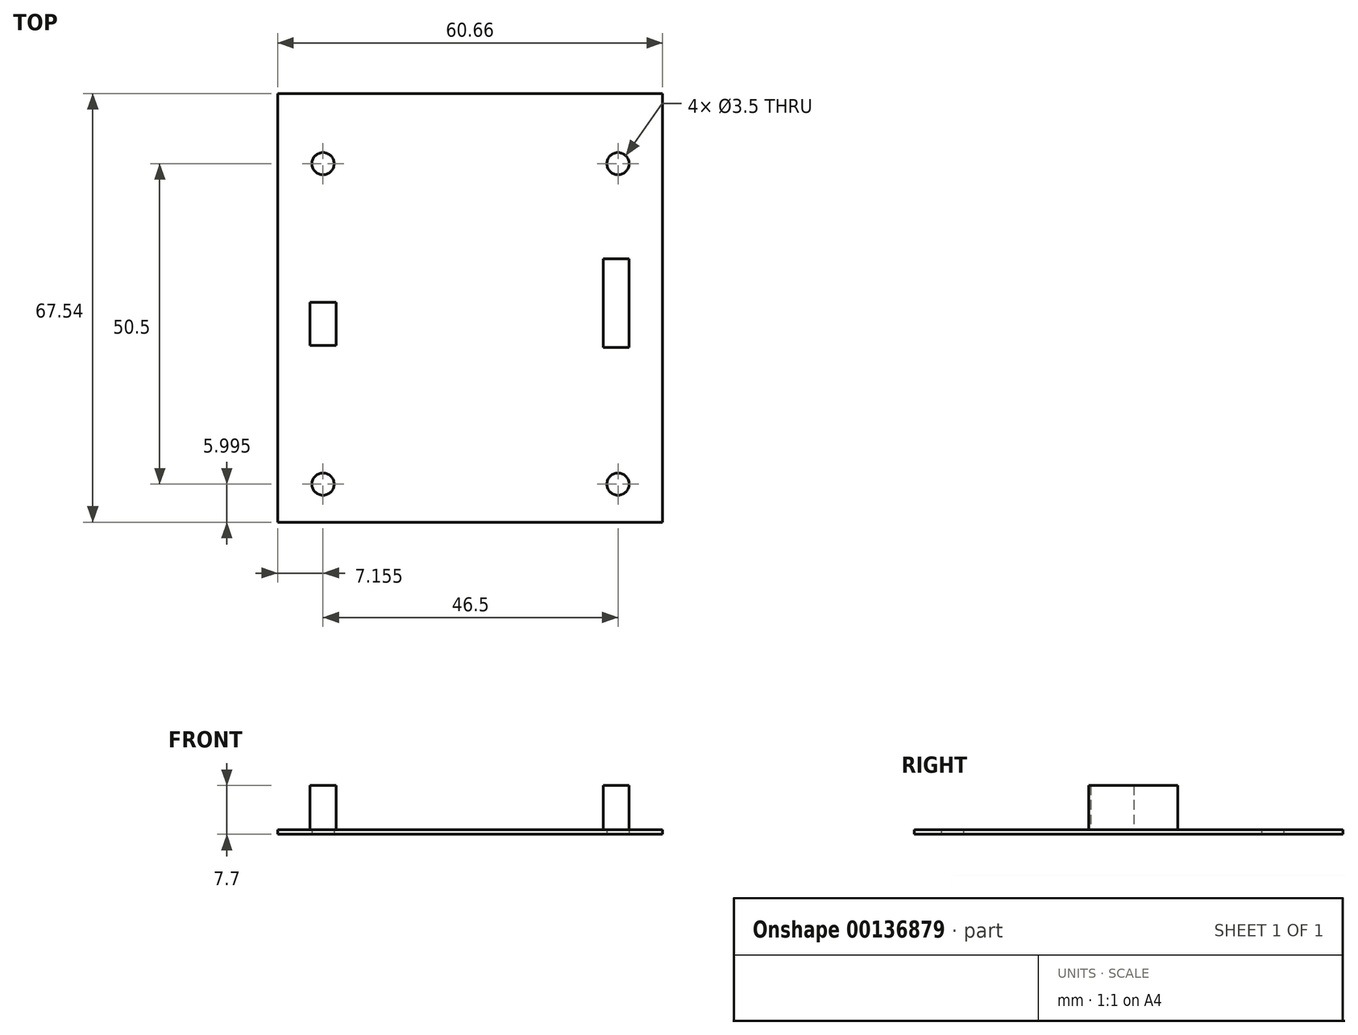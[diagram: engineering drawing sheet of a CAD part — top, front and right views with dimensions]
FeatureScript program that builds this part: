
annotation { "Feature Type Name" : "Feature", "Feature Type Description" : "" }
export const myFeature = defineFeature(function(context is Context, id is Id, definition is map)
    precondition{}
    {
        {
            var Q0;
            Q0=qCreatedBy(makeId("Top.planeOp"),FACE);
            var sketch = newSketch(context, id + "F0", { "sketchPlane" : qUnion([Q0])});
            skLineSegment(sketch, "E0.bottom", {"start": v(-30.32, 33.77) * mm, "end": v(30.33, 33.77) * mm});
            skLineSegment(sketch, "E0.top", {"start": v(-30.33, -33.77) * mm, "end": v(30.32, -33.77) * mm});
            skLineSegment(sketch, "E0.left", {"start": v(-30.32, 33.77) * mm, "end": v(-30.33, -33.77) * mm});
            skLineSegment(sketch, "E0.right", {"start": v(30.33, 33.77) * mm, "end": v(30.32, -33.77) * mm});
            skPoint(sketch, "E0.middle", {"position": v(0, 0) * mm});
            skCircle(sketch, "E1", {"center": v(23.32, -27.77) * mm, "radius": 1.75 * mm});
            skCircle(sketch, "E2", {"center": v(-23.18, -27.77) * mm, "radius": 1.75 * mm});
            skCircle(sketch, "E3", {"center": v(23.32, 22.73) * mm, "radius": 1.75 * mm});
            skCircle(sketch, "E4", {"center": v(-23.18, 22.73) * mm, "radius": 1.75 * mm});
            skSolve(sketch);
        }
        {
            var Q0;
            Q0=makeQuery(id+"F0.imprint","IMPRINT",FACE,{"disambiguationData":[TD([[makeQuery(id+"F0.imprint","IMPRINT",EDGE,{"derivedFrom":sQuery(id+"F0.wireOp",EDGE,"E0.bottom")}),-1.0]])]});
            extrude(context, id + "F1", {"entities" : qUnion([Q0]), "depth" : 0.7 * mm});
        }
        {
            var Q0;
            Q0=makeQuery(id+"F1.opExtrude","CAP_FACE",FACE,{"disambiguationData":[OSD([sQuery(id+"F0.wireOp",EDGE,"E0.bottom"),sQuery(id+"F0.wireOp",EDGE,"E0.top"),sQuery(id+"F0.wireOp",EDGE,"E0.left"),sQuery(id+"F0.wireOp",EDGE,"E0.right"),sQuery(id+"F0.wireOp",EDGE,"E1"),sQuery(id+"F0.wireOp",EDGE,"E2"),sQuery(id+"F0.wireOp",EDGE,"E3"),sQuery(id+"F0.wireOp",EDGE,"E4")])],"isStart":false});
            var sketch = newSketch(context, id + "F2", { "sketchPlane" : qUnion([Q0])});
            skLineSegment(sketch, "E5", {"start": v(23.32, -27.77) * mm, "end": v(25.07, -27.77) * mm});
            skLineSegment(sketch, "E6", {"start": v(25.07, 7.75) * mm, "end": v(20.97, 7.75) * mm});
            skLineSegment(sketch, "E7", {"start": v(20.97, 7.75) * mm, "end": v(20.97, -6.24) * mm});
            skLineSegment(sketch, "E8", {"start": v(20.97, -6.24) * mm, "end": v(25.07, -6.24) * mm});
            skLineSegment(sketch, "E9", {"start": v(25.07, -6.24) * mm, "end": v(25.07, 7.75) * mm});
            skLineSegment(sketch, "E10.bottom", {"start": v(-21.1, 0.87) * mm, "end": v(-25.25, 0.87) * mm});
            skLineSegment(sketch, "E10.top", {"start": v(-21.1, -5.92) * mm, "end": v(-25.25, -5.92) * mm});
            skLineSegment(sketch, "E10.left", {"start": v(-21.1, 0.87) * mm, "end": v(-21.1, -5.92) * mm});
            skLineSegment(sketch, "E10.right", {"start": v(-25.25, 0.87) * mm, "end": v(-25.25, -5.92) * mm});
            skPoint(sketch, "E10.middle", {"position": v(-23.18, -2.52) * mm});
            skSolve(sketch);
        }
        {
            var Q0;
            Q0=makeQuery(id+"F2.imprint","IMPRINT",FACE,{"disambiguationData":[TD([[makeQuery(id+"F2.imprint","IMPRINT",EDGE,{"derivedFrom":sQuery(id+"F2.wireOp",EDGE,"E10.bottom")}),1.0]])]});
            var Q1;
            Q1=makeQuery(id+"F2.imprint","IMPRINT",FACE,{"disambiguationData":[TD([[makeQuery(id+"F2.imprint","IMPRINT",EDGE,{"derivedFrom":sQuery(id+"F2.wireOp",EDGE,"E6")}),1.0]])]});
            extrude(context, id + "F3", {"entities" : qUnion([Q0, Q1]), "depth" : 7 * mm});
        }
    });
